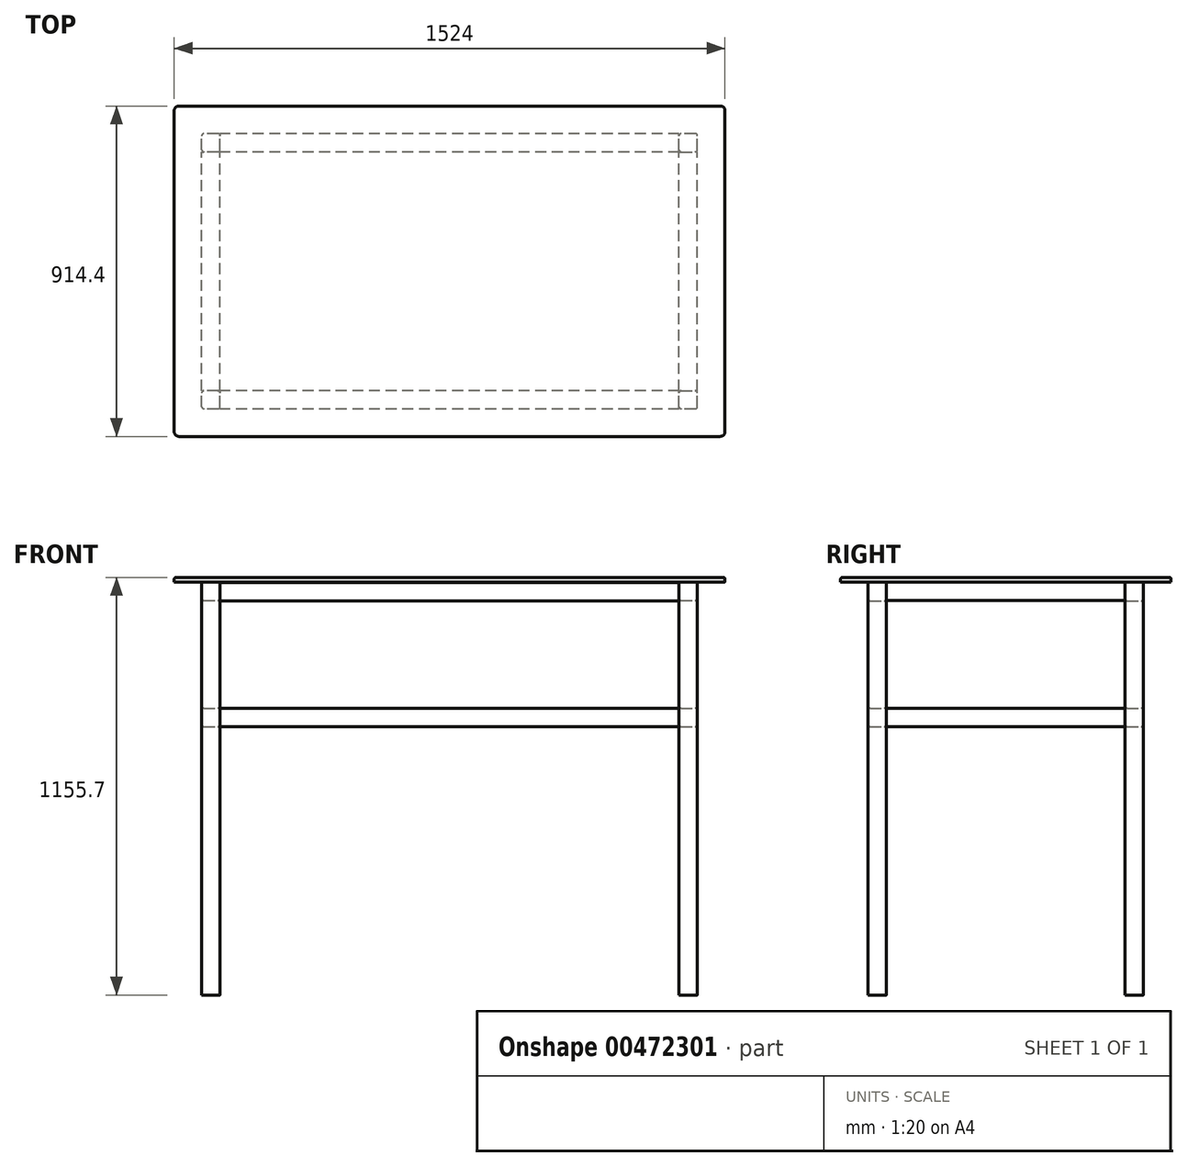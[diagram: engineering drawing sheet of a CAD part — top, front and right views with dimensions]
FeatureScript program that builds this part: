
annotation { "Feature Type Name" : "Feature", "Feature Type Description" : "" }
export const myFeature = defineFeature(function(context is Context, id is Id, definition is map)
    precondition{}
    {
        {
            var Q0;
            Q0=qCreatedBy(makeId("Top.planeOp"),FACE);
            var sketch = newSketch(context, id + "F0", { "sketchPlane" : qUnion([Q0])});
            skLineSegment(sketch, "E0.bottom", {"start": v(-762, -457.2) * mm, "end": v(762, -457.2) * mm});
            skLineSegment(sketch, "E0.top", {"start": v(-762, 457.2) * mm, "end": v(762, 457.2) * mm});
            skLineSegment(sketch, "E0.left", {"start": v(-762, -457.2) * mm, "end": v(-762, 457.2) * mm});
            skLineSegment(sketch, "E0.right", {"start": v(762, -457.2) * mm, "end": v(762, 457.2) * mm});
            skPoint(sketch, "E0.middle", {"position": v(0, 0) * mm});
            skLineSegment(sketch, "E1.bottom", {"start": v(-635, 330.2) * mm, "end": v(-685.8, 330.2) * mm});
            skLineSegment(sketch, "E1.top", {"start": v(-635, 381) * mm, "end": v(-685.8, 381) * mm});
            skLineSegment(sketch, "E1.left", {"start": v(-635, 330.2) * mm, "end": v(-635, 381) * mm});
            skLineSegment(sketch, "E1.right", {"start": v(-685.8, 330.2) * mm, "end": v(-685.8, 381) * mm});
            skPoint(sketch, "E1.middle", {"position": v(-660.4, 355.6) * mm});
            skLineSegment(sketch, "E2.0.1.0", {"start": v(-635, -330.2) * mm, "end": v(-685.8, -330.2) * mm});
            skLineSegment(sketch, "E2.0.1.1", {"start": v(-635, -381) * mm, "end": v(-635, -330.2) * mm});
            skLineSegment(sketch, "E2.0.1.2", {"start": v(-635, -381) * mm, "end": v(-685.8, -381) * mm});
            skLineSegment(sketch, "E2.0.1.3", {"start": v(-685.8, -381) * mm, "end": v(-685.8, -330.2) * mm});
            skPoint(sketch, "E2.0.1.4", {"position": v(-660.4, -355.6) * mm});
            skLineSegment(sketch, "E2.1.0.0", {"start": v(685.8, 381) * mm, "end": v(635, 381) * mm});
            skLineSegment(sketch, "E2.1.0.1", {"start": v(685.8, 330.2) * mm, "end": v(685.8, 381) * mm});
            skLineSegment(sketch, "E2.1.0.2", {"start": v(685.8, 330.2) * mm, "end": v(635, 330.2) * mm});
            skLineSegment(sketch, "E2.1.0.3", {"start": v(635, 330.2) * mm, "end": v(635, 381) * mm});
            skPoint(sketch, "E2.1.0.4", {"position": v(660.4, 355.6) * mm});
            skLineSegment(sketch, "E2.1.1.0", {"start": v(685.8, -330.2) * mm, "end": v(635, -330.2) * mm});
            skLineSegment(sketch, "E2.1.1.1", {"start": v(685.8, -381) * mm, "end": v(685.8, -330.2) * mm});
            skLineSegment(sketch, "E2.1.1.2", {"start": v(685.8, -381) * mm, "end": v(635, -381) * mm});
            skLineSegment(sketch, "E2.1.1.3", {"start": v(635, -381) * mm, "end": v(635, -330.2) * mm});
            skPoint(sketch, "E2.1.1.4", {"position": v(660.4, -355.6) * mm});
            skLineSegment(sketch, "E2.direction1", {"start": v(-635, 330.2) * mm, "end": v(685.8, 330.2) * mm, "construction": true});
            skLineSegment(sketch, "E2.direction2", {"start": v(-635, 330.2) * mm, "end": v(-635, -381) * mm, "construction": true});
            skSolve(sketch);
        }
        {
            var Q0;
            Q0 = qSketchRegion(id + "F0", true);
            var Q1;
            Q1=makeQuery(id+"F0.imprint","IMPRINT",FACE,{"disambiguationData":[TD([[makeQuery(id+"F0.imprint","IMPRINT",EDGE,{"derivedFrom":sQuery(id+"F0.wireOp",EDGE,"E1.bottom")}),-1.0]])]});
            var Q2;
            Q2=makeQuery(id+"F0.imprint","IMPRINT",FACE,{"disambiguationData":[TD([[makeQuery(id+"F0.imprint","IMPRINT",EDGE,{"derivedFrom":sQuery(id+"F0.wireOp",EDGE,"E2.0.1.0")}),1.0]])]});
            var Q3;
            Q3=makeQuery(id+"F0.imprint","IMPRINT",FACE,{"disambiguationData":[TD([[makeQuery(id+"F0.imprint","IMPRINT",EDGE,{"derivedFrom":sQuery(id+"F0.wireOp",EDGE,"E2.1.1.0")}),1.0]])]});
            var Q4;
            Q4=makeQuery(id+"F0.imprint","IMPRINT",FACE,{"disambiguationData":[TD([[makeQuery(id+"F0.imprint","IMPRINT",EDGE,{"derivedFrom":sQuery(id+"F0.wireOp",EDGE,"E2.1.0.0")}),1.0]])]});
            extrude(context, id + "F1", {"entities" : qUnion([Q0, Q1, Q2, Q3, Q4]), "depth" : 12.7 * mm});
        }
        {
            var Q0;
            Q0=makeQuery(id+"F0.imprint","IMPRINT",FACE,{"disambiguationData":[TD([[makeQuery(id+"F0.imprint","IMPRINT",EDGE,{"derivedFrom":sQuery(id+"F0.wireOp",EDGE,"E1.bottom")}),-1.0]])]});
            var Q1;
            Q1=makeQuery(id+"F0.imprint","IMPRINT",FACE,{"disambiguationData":[TD([[makeQuery(id+"F0.imprint","IMPRINT",EDGE,{"derivedFrom":sQuery(id+"F0.wireOp",EDGE,"E2.0.1.0")}),1.0]])]});
            var Q2;
            Q2=makeQuery(id+"F0.imprint","IMPRINT",FACE,{"disambiguationData":[TD([[makeQuery(id+"F0.imprint","IMPRINT",EDGE,{"derivedFrom":sQuery(id+"F0.wireOp",EDGE,"E2.1.1.0")}),1.0]])]});
            var Q3;
            Q3=makeQuery(id+"F0.imprint","IMPRINT",FACE,{"disambiguationData":[TD([[makeQuery(id+"F0.imprint","IMPRINT",EDGE,{"derivedFrom":sQuery(id+"F0.wireOp",EDGE,"E2.1.0.0")}),1.0]])]});
            extrude(context, id + "F2", {"entities" : qUnion([Q0, Q1, Q2, Q3]), "operationType" : NewBodyOperationType.ADD, "oppositeDirection" : true, "depth" : 1143 * mm});
        }
        {
            var Q0;
            Q0=makeQuery(id+"F1.opExtrude","SWEPT_EDGE",EDGE,{"disambiguationData":[OSD([sQuery(id+"F0.wireOp",EDGE,"E0.top"),sQuery(id+"F0.wireOp",EDGE,"E0.left")])]});
            var Q1;
            Q1=makeQuery(id+"F1.opExtrude","SWEPT_EDGE",EDGE,{"disambiguationData":[OSD([sQuery(id+"F0.wireOp",EDGE,"E0.bottom"),sQuery(id+"F0.wireOp",EDGE,"E0.left")])]});
            var Q2;
            Q2=makeQuery(id+"F1.opExtrude","SWEPT_EDGE",EDGE,{"disambiguationData":[OSD([sQuery(id+"F0.wireOp",EDGE,"E0.top"),sQuery(id+"F0.wireOp",EDGE,"E0.right")])]});
            var Q3;
            Q3=makeQuery(id+"F1.opExtrude","SWEPT_EDGE",EDGE,{"disambiguationData":[OSD([sQuery(id+"F0.wireOp",EDGE,"E0.bottom"),sQuery(id+"F0.wireOp",EDGE,"E0.right")])]});
            fillet(context, id + "F3", {"entities" : qUnion([Q0, Q1, Q2, Q3]), "radius" : 12.7 * mm, "tangentPropagation" : true, "allowEdgeOverflow" : false});
        }
        {
            var Q0;
            Q0=makeQuery(id+"F1.opExtrude","CAP_EDGE",EDGE,{"disambiguationData":[OSD([sQuery(id+"F0.wireOp",EDGE,"E0.right")])],"isStart":false});
            var Q1;
            Q1=makeQuery(id+"F1.opExtrude","CAP_EDGE",EDGE,{"disambiguationData":[OSD([sQuery(id+"F0.wireOp",EDGE,"E0.top")])],"isStart":false});
            var Q2;
            Q2=makeQuery(id+"F1.opExtrude","CAP_FACE",FACE,{"disambiguationData":[OSD([sQuery(id+"F0.wireOp",EDGE,"E0.bottom"),sQuery(id+"F0.wireOp",EDGE,"E0.top"),sQuery(id+"F0.wireOp",EDGE,"E0.left"),sQuery(id+"F0.wireOp",EDGE,"E0.right")])],"isStart":false});
            var Q3;
            Q3=makeQuery(id+"F1.opExtrude","CAP_EDGE",EDGE,{"disambiguationData":[OSD([sQuery(id+"F0.wireOp",EDGE,"E0.bottom")])],"isStart":false});
            var Q4;
            {var subQ0=sQuery(id+"F0.wireOp",EDGE,"E0.right");var subQ1=sQuery(id+"F0.wireOp",EDGE,"E0.bottom");Q4=makeQuery(id+"F3.opFillet","BLEND_EDGE",EDGE,{"blendedFrom":[makeQuery(id+"F1.opExtrude","SWEPT_EDGE",EDGE,{"disambiguationData":[OSD([subQ1,subQ0])]}),makeQuery(id+"F1.opExtrude","CAP_FACE",FACE,{"disambiguationData":[OSD([subQ1,sQuery(id+"F0.wireOp",EDGE,"E0.top"),sQuery(id+"F0.wireOp",EDGE,"E0.left"),subQ0])],"isStart":false})],"blendedInto":[makeQuery(id+"F1.opExtrude","CAP_FACE",FACE,{"disambiguationData":[OSD([subQ1,sQuery(id+"F0.wireOp",EDGE,"E0.top"),sQuery(id+"F0.wireOp",EDGE,"E0.left"),subQ0])],"isStart":false})]});}
            var Q5;
            {var subQ0=sQuery(id+"F0.wireOp",EDGE,"E0.right");var subQ1=sQuery(id+"F0.wireOp",EDGE,"E0.top");Q5=makeQuery(id+"F3.opFillet","BLEND_EDGE",EDGE,{"blendedFrom":[makeQuery(id+"F1.opExtrude","SWEPT_EDGE",EDGE,{"disambiguationData":[OSD([subQ1,subQ0])]}),makeQuery(id+"F1.opExtrude","CAP_FACE",FACE,{"disambiguationData":[OSD([sQuery(id+"F0.wireOp",EDGE,"E0.bottom"),subQ1,sQuery(id+"F0.wireOp",EDGE,"E0.left"),subQ0])],"isStart":false})],"blendedInto":[makeQuery(id+"F1.opExtrude","CAP_FACE",FACE,{"disambiguationData":[OSD([sQuery(id+"F0.wireOp",EDGE,"E0.bottom"),subQ1,sQuery(id+"F0.wireOp",EDGE,"E0.left"),subQ0])],"isStart":false})]});}
            var Q6;
            Q6=makeQuery(id+"F1.opExtrude","CAP_EDGE",EDGE,{"disambiguationData":[OSD([sQuery(id+"F0.wireOp",EDGE,"E0.left")])],"isStart":false});
            var Q7;
            {var subQ0=sQuery(id+"F0.wireOp",EDGE,"E0.left");var subQ1=sQuery(id+"F0.wireOp",EDGE,"E0.top");Q7=makeQuery(id+"F3.opFillet","BLEND_EDGE",EDGE,{"blendedFrom":[makeQuery(id+"F1.opExtrude","SWEPT_EDGE",EDGE,{"disambiguationData":[OSD([subQ1,subQ0])]}),makeQuery(id+"F1.opExtrude","CAP_FACE",FACE,{"disambiguationData":[OSD([sQuery(id+"F0.wireOp",EDGE,"E0.bottom"),subQ1,subQ0,sQuery(id+"F0.wireOp",EDGE,"E0.right")])],"isStart":false})],"blendedInto":[makeQuery(id+"F1.opExtrude","CAP_FACE",FACE,{"disambiguationData":[OSD([sQuery(id+"F0.wireOp",EDGE,"E0.bottom"),subQ1,subQ0,sQuery(id+"F0.wireOp",EDGE,"E0.right")])],"isStart":false})]});}
            var Q8;
            {var subQ0=sQuery(id+"F0.wireOp",EDGE,"E0.left");var subQ1=sQuery(id+"F0.wireOp",EDGE,"E0.bottom");Q8=makeQuery(id+"F3.opFillet","BLEND_EDGE",EDGE,{"blendedFrom":[makeQuery(id+"F1.opExtrude","SWEPT_EDGE",EDGE,{"disambiguationData":[OSD([subQ1,subQ0])]}),makeQuery(id+"F1.opExtrude","CAP_FACE",FACE,{"disambiguationData":[OSD([subQ1,sQuery(id+"F0.wireOp",EDGE,"E0.top"),subQ0,sQuery(id+"F0.wireOp",EDGE,"E0.right")])],"isStart":false})],"blendedInto":[makeQuery(id+"F1.opExtrude","CAP_FACE",FACE,{"disambiguationData":[OSD([subQ1,sQuery(id+"F0.wireOp",EDGE,"E0.top"),subQ0,sQuery(id+"F0.wireOp",EDGE,"E0.right")])],"isStart":false})]});}
            fillet(context, id + "F4", {"entities" : qUnion([Q0, Q1, Q2, Q3, Q4, Q5, Q6, Q7, Q8]), "radius" : 5.08 * mm, "tangentPropagation" : true, "allowEdgeOverflow" : false});
        }
        {
            var Q0;
            Q0=makeQuery(id+"F2.opExtrude","SWEPT_EDGE",EDGE,{"disambiguationData":[OSD([sQuery(id+"F0.wireOp",EDGE,"E2.0.1.2"),sQuery(id+"F0.wireOp",EDGE,"E2.0.1.3")])]});
            var Q1;
            Q1=makeQuery(id+"F2.opExtrude","SWEPT_EDGE",EDGE,{"disambiguationData":[OSD([sQuery(id+"F0.wireOp",EDGE,"E2.0.1.1"),sQuery(id+"F0.wireOp",EDGE,"E2.0.1.2")])]});
            var Q2;
            Q2=makeQuery(id+"F2.opExtrude","SWEPT_EDGE",EDGE,{"disambiguationData":[OSD([sQuery(id+"F0.wireOp",EDGE,"E2.0.1.0"),sQuery(id+"F0.wireOp",EDGE,"E2.0.1.3")])]});
            var Q3;
            Q3=makeQuery(id+"F2.opExtrude","SWEPT_EDGE",EDGE,{"disambiguationData":[OSD([sQuery(id+"F0.wireOp",EDGE,"E1.bottom"),sQuery(id+"F0.wireOp",EDGE,"E1.left")])]});
            var Q4;
            Q4=makeQuery(id+"F2.opExtrude","SWEPT_EDGE",EDGE,{"disambiguationData":[OSD([sQuery(id+"F0.wireOp",EDGE,"E1.bottom"),sQuery(id+"F0.wireOp",EDGE,"E1.right")])]});
            var Q5;
            Q5=makeQuery(id+"F2.opExtrude","SWEPT_EDGE",EDGE,{"disambiguationData":[OSD([sQuery(id+"F0.wireOp",EDGE,"E1.top"),sQuery(id+"F0.wireOp",EDGE,"E1.right")])]});
            var Q6;
            Q6=makeQuery(id+"F2.opExtrude","SWEPT_EDGE",EDGE,{"disambiguationData":[OSD([sQuery(id+"F0.wireOp",EDGE,"E2.1.1.2"),sQuery(id+"F0.wireOp",EDGE,"E2.1.1.3")])]});
            var Q7;
            Q7=makeQuery(id+"F2.opExtrude","SWEPT_EDGE",EDGE,{"disambiguationData":[OSD([sQuery(id+"F0.wireOp",EDGE,"E2.1.1.1"),sQuery(id+"F0.wireOp",EDGE,"E2.1.1.2")])]});
            var Q8;
            Q8=makeQuery(id+"F2.opExtrude","SWEPT_EDGE",EDGE,{"disambiguationData":[OSD([sQuery(id+"F0.wireOp",EDGE,"E2.1.1.0"),sQuery(id+"F0.wireOp",EDGE,"E2.1.1.3")])]});
            var Q9;
            Q9=makeQuery(id+"F2.opExtrude","SWEPT_EDGE",EDGE,{"disambiguationData":[OSD([sQuery(id+"F0.wireOp",EDGE,"E2.1.0.2"),sQuery(id+"F0.wireOp",EDGE,"E2.1.0.3")])]});
            var Q10;
            Q10=makeQuery(id+"F2.opExtrude","SWEPT_EDGE",EDGE,{"disambiguationData":[OSD([sQuery(id+"F0.wireOp",EDGE,"E2.1.0.1"),sQuery(id+"F0.wireOp",EDGE,"E2.1.0.2")])]});
            var Q11;
            Q11=makeQuery(id+"F2.opExtrude","SWEPT_EDGE",EDGE,{"disambiguationData":[OSD([sQuery(id+"F0.wireOp",EDGE,"E2.1.0.0"),sQuery(id+"F0.wireOp",EDGE,"E2.1.0.3")])]});
            var Q12;
            Q12=makeQuery(id+"F2.opExtrude","SWEPT_EDGE",EDGE,{"disambiguationData":[OSD([sQuery(id+"F0.wireOp",EDGE,"E2.1.1.0"),sQuery(id+"F0.wireOp",EDGE,"E2.1.1.1")])]});
            var Q13;
            Q13=makeQuery(id+"F2.opExtrude","SWEPT_EDGE",EDGE,{"disambiguationData":[OSD([sQuery(id+"F0.wireOp",EDGE,"E2.1.0.0"),sQuery(id+"F0.wireOp",EDGE,"E2.1.0.1")])]});
            var Q14;
            Q14=makeQuery(id+"F2.opExtrude","SWEPT_EDGE",EDGE,{"disambiguationData":[OSD([sQuery(id+"F0.wireOp",EDGE,"E1.top"),sQuery(id+"F0.wireOp",EDGE,"E1.left")])]});
            var Q15;
            Q15=makeQuery(id+"F2.opExtrude","SWEPT_EDGE",EDGE,{"disambiguationData":[OSD([sQuery(id+"F0.wireOp",EDGE,"E2.0.1.0"),sQuery(id+"F0.wireOp",EDGE,"E2.0.1.1")])]});
            fillet(context, id + "F5", {"entities" : qUnion([Q0, Q1, Q2, Q3, Q4, Q5, Q6, Q7, Q8, Q9, Q10, Q11, Q12, Q13, Q14, Q15]), "radius" : 6.35 * mm, "tangentPropagation" : true, "allowEdgeOverflow" : false});
        }
        {
            var Q0;
            Q0=makeQuery(id+"F2.opExtrude","SWEPT_FACE",FACE,{"disambiguationData":[OSD([sQuery(id+"F0.wireOp",EDGE,"E2.1.0.0")])]});
            var sketch = newSketch(context, id + "F6", { "sketchPlane" : qUnion([Q0])});
            skLineSegment(sketch, "E3.bottom", {"start": v(-635, -349.3) * mm, "end": v(635, -349.3) * mm});
            skLineSegment(sketch, "E3.top", {"start": v(-635, -400.1) * mm, "end": v(635, -400.1) * mm});
            skLineSegment(sketch, "E3.left", {"start": v(-635, -349.3) * mm, "end": v(-635, -400.1) * mm});
            skLineSegment(sketch, "E3.right", {"start": v(635, -349.3) * mm, "end": v(635, -400.1) * mm});
            skSolve(sketch);
        }
        {
            var Q0;
            Q0 = qSketchRegion(id + "F6", true);
            extrude(context, id + "F7", {"entities" : qUnion([Q0]), "oppositeDirection" : true, "depth" : 50.8 * mm});
        }
        {
            var Q0;
            Q0=makeQuery(id+"F7.opExtrude","CAP_EDGE",EDGE,{"disambiguationData":[OSD([sQuery(id+"F6.wireOp",EDGE,"E3.bottom")])],"isStart":true});
            var Q1;
            Q1=makeQuery(id+"F7.opExtrude","CAP_EDGE",EDGE,{"disambiguationData":[OSD([sQuery(id+"F6.wireOp",EDGE,"E3.top")])],"isStart":true});
            var Q2;
            Q2=makeQuery(id+"F7.opExtrude","CAP_EDGE",EDGE,{"disambiguationData":[OSD([sQuery(id+"F6.wireOp",EDGE,"E3.bottom")])],"isStart":false});
            var Q3;
            Q3=makeQuery(id+"F7.opExtrude","CAP_EDGE",EDGE,{"disambiguationData":[OSD([sQuery(id+"F6.wireOp",EDGE,"E3.top")])],"isStart":false});
            fillet(context, id + "F8", {"entities" : qUnion([Q0, Q1, Q2, Q3]), "radius" : 6.35 * mm, "tangentPropagation" : true, "allowEdgeOverflow" : false});
        }
        {
            var Q0;
            Q0=makeQuery(id+"F7.opExtrude","SWEPT_BODY",BODY,{"disambiguationData":[OSD([sQuery(id+"F6.wireOp",EDGE,"E3.bottom"),sQuery(id+"F6.wireOp",EDGE,"E3.top"),sQuery(id+"F6.wireOp",EDGE,"E3.left"),sQuery(id+"F6.wireOp",EDGE,"E3.right")])]});
            transform(context, id + "F9", {"entities" : qUnion([Q0]), "transformType" : TransformType.TRANSLATION_3D, "dx" : 0 * mm, "dy" : -711.2 * mm, "dz" : 0 * mm, "makeCopy" : true});
        }
        {
            var Q0;
            Q0=makeQuery(id+"F7.opExtrude","SWEPT_BODY",BODY,{"disambiguationData":[OSD([sQuery(id+"F6.wireOp",EDGE,"E3.bottom"),sQuery(id+"F6.wireOp",EDGE,"E3.top"),sQuery(id+"F6.wireOp",EDGE,"E3.left"),sQuery(id+"F6.wireOp",EDGE,"E3.right")])]});
            transform(context, id + "F10", {"entities" : qUnion([Q0]), "transformType" : TransformType.TRANSLATION_3D, "dx" : 0 * mm, "dy" : 0 * mm, "dz" : 347.98 * mm, "makeCopy" : true});
        }
        {
            var Q0;
            Q0=makeQuery(id+"F10.opPattern","COPY",BODY,{"derivedFrom":makeQuery(id+"F7.opExtrude","SWEPT_BODY",BODY,{"disambiguationData":[OSD([sQuery(id+"F6.wireOp",EDGE,"E3.bottom"),sQuery(id+"F6.wireOp",EDGE,"E3.top"),sQuery(id+"F6.wireOp",EDGE,"E3.left"),sQuery(id+"F6.wireOp",EDGE,"E3.right")])]}),"instanceName":"1"});
            transform(context, id + "F11", {"entities" : qUnion([Q0]), "transformType" : TransformType.TRANSLATION_3D, "dx" : 0 * mm, "dy" : -711.2 * mm, "dz" : 0 * mm, "makeCopy" : true});
        }
        {
            var Q0;
            Q0=makeQuery(id+"F7.opExtrude","SWEPT_BODY",BODY,{"disambiguationData":[OSD([sQuery(id+"F6.wireOp",EDGE,"E3.bottom"),sQuery(id+"F6.wireOp",EDGE,"E3.top"),sQuery(id+"F6.wireOp",EDGE,"E3.left"),sQuery(id+"F6.wireOp",EDGE,"E3.right")])]});
            transform(context, id + "F12", {"entities" : qUnion([Q0]), "transformType" : TransformType.TRANSLATION_3D, "dx" : 0 * mm, "dy" : 416.56 * mm, "dz" : 0 * mm, "makeCopy" : true});
        }
        {
            var Q0;
            Q0=makeQuery(id+"F12.opPattern","COPY",BODY,{"derivedFrom":makeQuery(id+"F7.opExtrude","SWEPT_BODY",BODY,{"disambiguationData":[OSD([sQuery(id+"F6.wireOp",EDGE,"E3.bottom"),sQuery(id+"F6.wireOp",EDGE,"E3.top"),sQuery(id+"F6.wireOp",EDGE,"E3.left"),sQuery(id+"F6.wireOp",EDGE,"E3.right")])]}),"instanceName":"1"});
            var Q1;
            Q1=makeQuery(id+"F12.opPattern","COPY",EDGE,{"derivedFrom":makeQuery(id+"F7.opExtrude","CAP_EDGE",EDGE,{"disambiguationData":[OSD([sQuery(id+"F6.wireOp",EDGE,"E3.right")])],"isStart":false}),"instanceName":"1"});
            transform(context, id + "F13", {"entities" : qUnion([Q0]), "transformType" : TransformType.ROTATION, "transformAxis" : qUnion([Q1]), "angle" : 90 * degree, "makeCopy" : false});
        }
        {
            var Q0;
            Q0=makeQuery(id+"F12.opPattern","COPY",BODY,{"derivedFrom":makeQuery(id+"F7.opExtrude","SWEPT_BODY",BODY,{"disambiguationData":[OSD([sQuery(id+"F6.wireOp",EDGE,"E3.bottom"),sQuery(id+"F6.wireOp",EDGE,"E3.top"),sQuery(id+"F6.wireOp",EDGE,"E3.left"),sQuery(id+"F6.wireOp",EDGE,"E3.right")])]}),"instanceName":"1"});
            deleteBodies(context, id + "F14", {"entities" : qUnion([Q0])});
        }
        {
            var Q0;
            Q0=makeQuery(id+"F2.opExtrude","SWEPT_FACE",FACE,{"disambiguationData":[OSD([sQuery(id+"F0.wireOp",EDGE,"E2.1.1.1")])]});
            var sketch = newSketch(context, id + "F15", { "sketchPlane" : qUnion([Q0])});
            skLineSegment(sketch, "E4.bottom", {"start": v(-330.2, -349.25) * mm, "end": v(330.2, -349.25) * mm});
            skLineSegment(sketch, "E4.top", {"start": v(-330.2, -400.05) * mm, "end": v(330.2, -400.05) * mm});
            skLineSegment(sketch, "E4.left", {"start": v(-330.2, -349.25) * mm, "end": v(-330.2, -400.05) * mm});
            skLineSegment(sketch, "E4.right", {"start": v(330.2, -349.25) * mm, "end": v(330.2, -400.05) * mm});
            skSolve(sketch);
        }
        {
            var Q0;
            Q0 = qSketchRegion(id + "F15", true);
            extrude(context, id + "F16", {"entities" : qUnion([Q0]), "oppositeDirection" : true, "depth" : 50.8 * mm});
        }
        {
            var Q0;
            Q0=makeQuery(id+"F16.opExtrude","CAP_EDGE",EDGE,{"disambiguationData":[OSD([sQuery(id+"F15.wireOp",EDGE,"E4.bottom")])],"isStart":true});
            var Q1;
            Q1=makeQuery(id+"F16.opExtrude","CAP_EDGE",EDGE,{"disambiguationData":[OSD([sQuery(id+"F15.wireOp",EDGE,"E4.top")])],"isStart":true});
            var Q2;
            Q2=makeQuery(id+"F16.opExtrude","CAP_EDGE",EDGE,{"disambiguationData":[OSD([sQuery(id+"F15.wireOp",EDGE,"E4.bottom")])],"isStart":false});
            var Q3;
            Q3=makeQuery(id+"F16.opExtrude","CAP_EDGE",EDGE,{"disambiguationData":[OSD([sQuery(id+"F15.wireOp",EDGE,"E4.top")])],"isStart":false});
            fillet(context, id + "F17", {"entities" : qUnion([Q0, Q1, Q2, Q3]), "radius" : 6.35 * mm, "tangentPropagation" : true, "allowEdgeOverflow" : false});
        }
        {
            var Q0;
            Q0=makeQuery(id+"F16.opExtrude","SWEPT_BODY",BODY,{"disambiguationData":[OSD([sQuery(id+"F15.wireOp",EDGE,"E4.bottom"),sQuery(id+"F15.wireOp",EDGE,"E4.top"),sQuery(id+"F15.wireOp",EDGE,"E4.left"),sQuery(id+"F15.wireOp",EDGE,"E4.right")])]});
            transform(context, id + "F18", {"entities" : qUnion([Q0]), "transformType" : TransformType.TRANSLATION_3D, "dx" : 0 * mm, "dy" : 0 * mm, "dz" : 349.25 * mm, "makeCopy" : true});
        }
        {
            var Q0;
            Q0=makeQuery(id+"F16.opExtrude","SWEPT_BODY",BODY,{"disambiguationData":[OSD([sQuery(id+"F15.wireOp",EDGE,"E4.bottom"),sQuery(id+"F15.wireOp",EDGE,"E4.top"),sQuery(id+"F15.wireOp",EDGE,"E4.left"),sQuery(id+"F15.wireOp",EDGE,"E4.right")])]});
            transform(context, id + "F19", {"entities" : qUnion([Q0]), "transformType" : TransformType.TRANSLATION_3D, "dx" : -1320.8 * mm, "dy" : 0 * mm, "dz" : 0 * mm, "makeCopy" : true});
        }
        {
            var Q0;
            Q0=makeQuery(id+"F18.opPattern","COPY",BODY,{"derivedFrom":makeQuery(id+"F16.opExtrude","SWEPT_BODY",BODY,{"disambiguationData":[OSD([sQuery(id+"F15.wireOp",EDGE,"E4.bottom"),sQuery(id+"F15.wireOp",EDGE,"E4.top"),sQuery(id+"F15.wireOp",EDGE,"E4.left"),sQuery(id+"F15.wireOp",EDGE,"E4.right")])]}),"instanceName":"1"});
            transform(context, id + "F20", {"entities" : qUnion([Q0]), "transformType" : TransformType.TRANSLATION_3D, "dx" : -1320.8 * mm, "dy" : 0 * mm, "dz" : 0 * mm, "makeCopy" : true});
        }
    });
